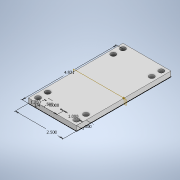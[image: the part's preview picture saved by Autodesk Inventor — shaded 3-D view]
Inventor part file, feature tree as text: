
AUTODESK INVENTOR PART (.ipt)
format: ipt  version: 2020 (Build 240168000, 168)  size: 117,248 bytes
history: native  units: in
note: dims shown in document units (in); Inventor stores cm internally (conversion verified against a paired STEP export)
features: sketch x1, extrude x1, hole x1, other x1, plane x1, mirror x1
ambient origin geometry x8: Origin, YZ Plane, XZ Plane, XY Plane, X Axis, Y Axis, Z Axis, Center Point
bodies: Solid1 (feature_tree)
feature tree (6):
  sketch  "Sketch1"  dims[d0=4.9213in d1=0.25in d2=1.0in d3=2.5in d4=1.25in d5=1.0in d6=0.5in d7=0.5in d8=0.25in d9=0.0in d10=0.266in d11=0.75in d12=0.438in d13=0.25in d14=0.5635in d15=0.224in d16=0.0in]
  extrude  "Extrusion1"  Depth=0.25in
  hole  "Hole1"  [1 undecoded]
  other  "Work Point1"
  plane  "Work Plane1"
  mirror  "Mirror1"
note: 1 required parameter value undecoded (feature->parameter linkage not recoverable at this tier; creation-order binding heuristic only, values carry confidence <= 0.55)
